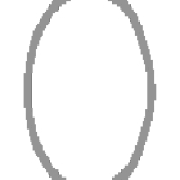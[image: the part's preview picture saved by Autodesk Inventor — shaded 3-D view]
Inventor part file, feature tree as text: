
AUTODESK INVENTOR PART (.ipt)
format: ipt  version: 2021 (Build 250183000, 183)  size: 129,024 bytes
history: native  units: in
note: dims shown in document units (in); Inventor stores cm internally (conversion verified against a paired STEP export)
features: other x4, plane x4, sketch x4, extrude x1, boolean_combine x1
ambient origin geometry x8: Origin, YZ Plane, XZ Plane, XY Plane, X Axis, Y Axis, Z Axis, Center Point
bodies: Solid1 (feature_tree), Body (feature_tree), Solid2 (feature_tree)
feature tree (14):
  other  "Driven Length"
  other  "Frame Generator"
  other  "Start Plane"
  other  "End Plane"
  plane  "Work Plane8"
  plane  "Work Plane9"
  plane  "Work Plane10"
  extrude  "Extrusion3"  Depth=0.049in
  boolean_combine  "Combine1"
  sketch  "Sketch"  dims[d5=5.831in d6=0.12in d7=0.0in d16=90.0deg d9=5.831in d18=0.12in d19=0.0in]
  sketch  "Sketch10"  dims[d0=1.0in d1=0.049in]
  plane  "Work Plane7"
  sketch  "Sketch11"  dims[d2=5.831in]
  sketch  "Sketch12"  dims[d4=-0.0in]
